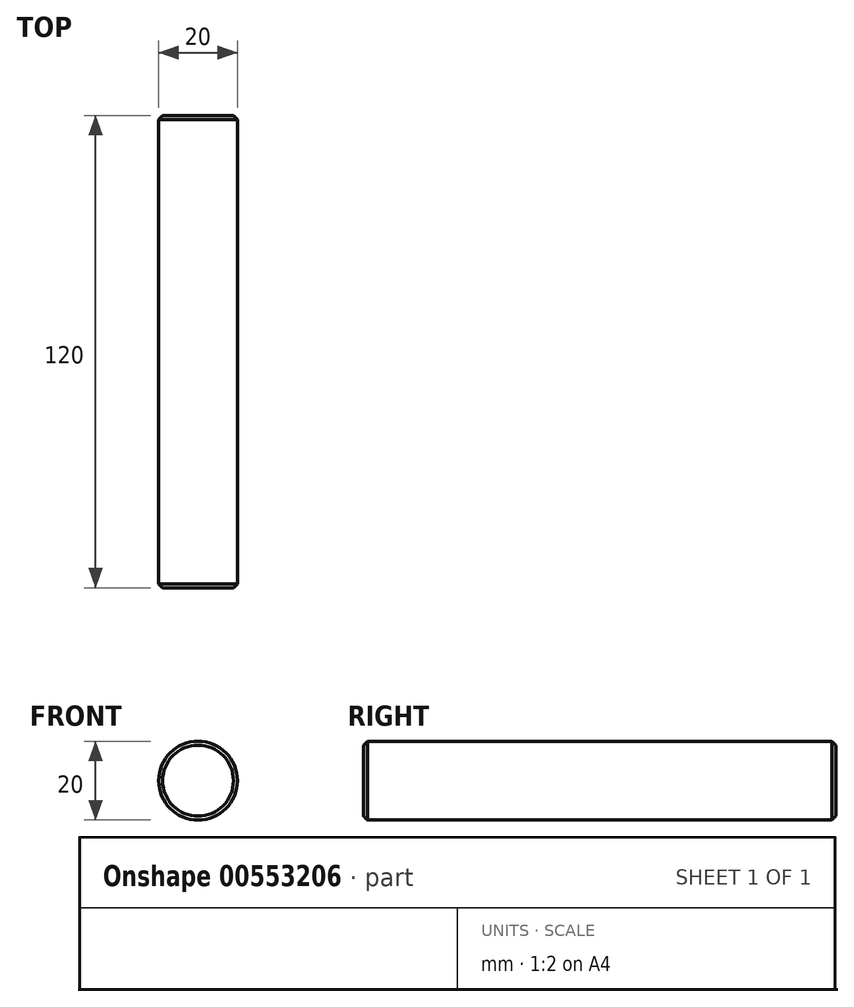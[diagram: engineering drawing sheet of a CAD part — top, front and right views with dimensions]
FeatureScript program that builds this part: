
annotation { "Feature Type Name" : "Feature", "Feature Type Description" : "" }
export const myFeature = defineFeature(function(context is Context, id is Id, definition is map)
    precondition{}
    {
        {
            var Q0;
            Q0=qCreatedBy(makeId("Front.planeOp"),FACE);
            var sketch = newSketch(context, id + "F0", { "sketchPlane" : qUnion([Q0])});
            skCircle(sketch, "E0", {"center": v(0, 0) * mm, "radius": 10 * mm});
            skSolve(sketch);
        }
        {
            var Q0;
            Q0 = qSketchRegion(id + "F0", true);
            extrude(context, id + "F1", {"entities" : qUnion([Q0]), "endBound" : BoundingType.SYMMETRIC, "depth" : 120 * mm, "offsetDistance" : 25 * mm});
        }
        {
            var Q0;
            Q0=makeQuery(id+"F1.opExtrude","CAP_EDGE",EDGE,{"disambiguationData":[OSD([sQuery(id+"F0.wireOp",EDGE,"E0")])],"isStart":false});
            var Q1;
            Q1=makeQuery(id+"F1.opExtrude","CAP_EDGE",EDGE,{"disambiguationData":[OSD([sQuery(id+"F0.wireOp",EDGE,"E0")])],"isStart":true});
            chamfer(context, id + "F2", {"entities" : qUnion([Q0, Q1]), "width" : 1 * mm, "tangentPropagation" : true});
        }
    });
